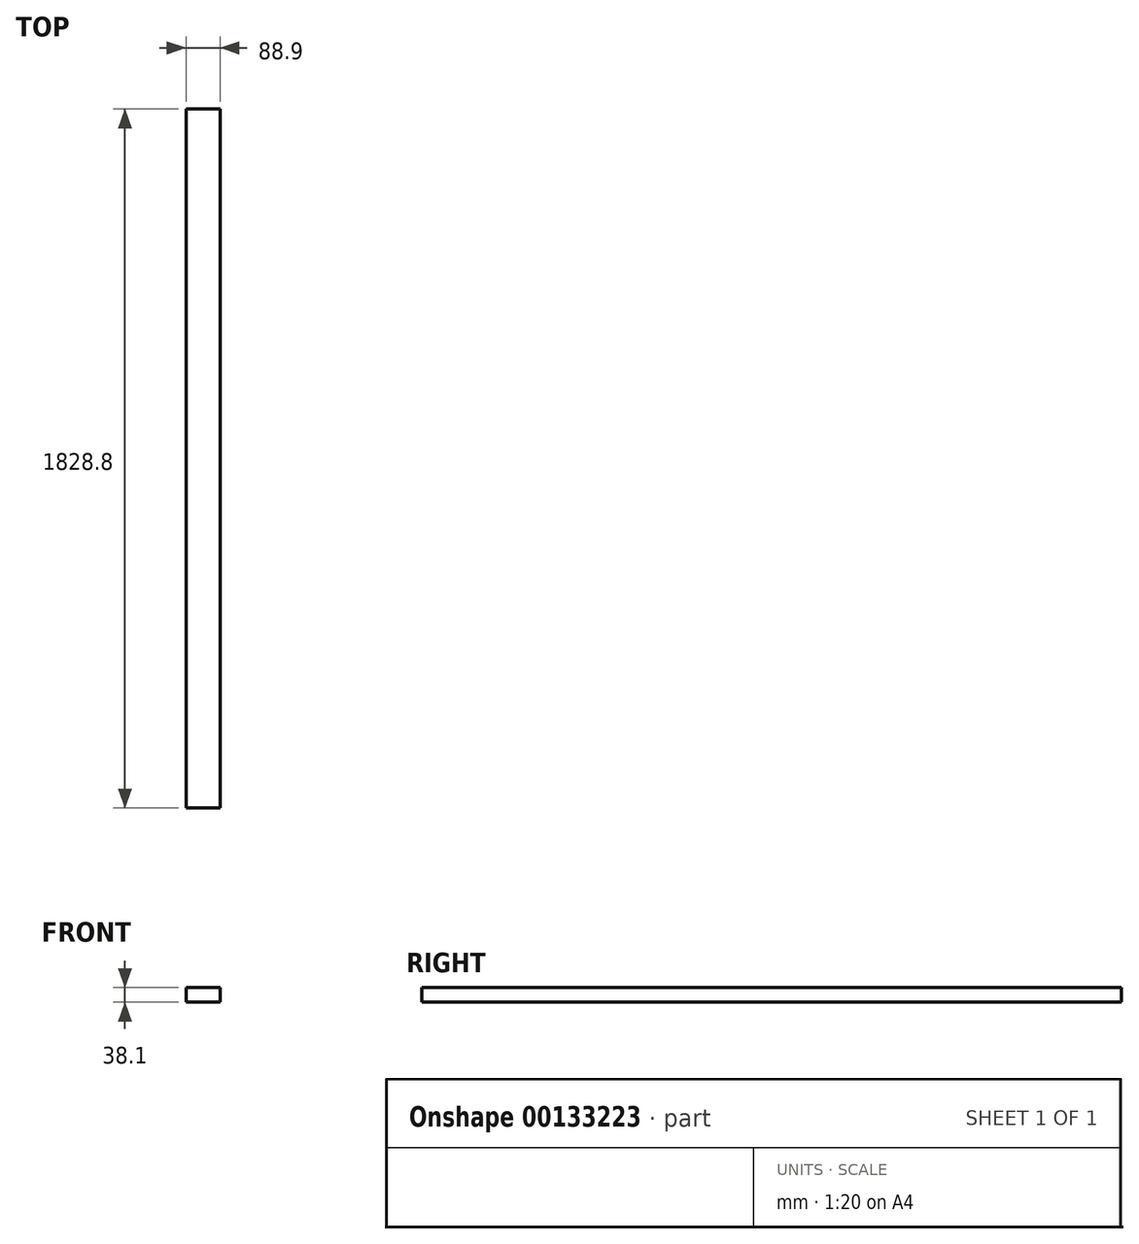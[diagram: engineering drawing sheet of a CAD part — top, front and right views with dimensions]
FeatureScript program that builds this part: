
annotation { "Feature Type Name" : "Feature", "Feature Type Description" : "" }
export const myFeature = defineFeature(function(context is Context, id is Id, definition is map)
    precondition{}
    {
        {
            var Q0;
            Q0=qCreatedBy(makeId("Front.planeOp"),FACE);
            var sketch = newSketch(context, id + "F0", { "sketchPlane" : qUnion([Q0])});
            skLineSegment(sketch, "E0.bottom", {"start": v(0, 0) * mm, "end": v(88.9, 0) * mm});
            skLineSegment(sketch, "E0.top", {"start": v(0, 38.1) * mm, "end": v(88.9, 38.1) * mm});
            skLineSegment(sketch, "E0.left", {"start": v(0, 0) * mm, "end": v(0, 38.1) * mm});
            skLineSegment(sketch, "E0.right", {"start": v(88.9, 0) * mm, "end": v(88.9, 38.1) * mm});
            skSolve(sketch);
        }
        {
            var Q0;
            Q0 = qSketchRegion(id + "F0", true);
            extrude(context, id + "F1", {"entities" : qUnion([Q0]), "depth" : 1828.8 * mm});
        }
        {
            var Q0;
            Q0=makeQuery(id+"F1.opExtrude","SWEPT_BODY",BODY,{"disambiguationData":[OSD([sQuery(id+"F0.wireOp",EDGE,"E0.bottom"),sQuery(id+"F0.wireOp",EDGE,"E0.top"),sQuery(id+"F0.wireOp",EDGE,"E0.left"),sQuery(id+"F0.wireOp",EDGE,"E0.right")])]});
            transform(context, id + "F2", {"entities" : qUnion([Q0]), "transformType" : TransformType.TRANSLATION_3D, "dx" : 203.2 * mm, "dy" : 0 * mm, "dz" : 0 * mm, "makeCopy" : true});
        }
        {
            var Q0;
            Q0=makeQuery(id+"F2.opPattern","COPY",BODY,{"derivedFrom":makeQuery(id+"F1.opExtrude","SWEPT_BODY",BODY,{"disambiguationData":[OSD([sQuery(id+"F0.wireOp",EDGE,"E0.bottom"),sQuery(id+"F0.wireOp",EDGE,"E0.top"),sQuery(id+"F0.wireOp",EDGE,"E0.left"),sQuery(id+"F0.wireOp",EDGE,"E0.right")])]}),"instanceName":"1"});
            deleteBodies(context, id + "F3", {"entities" : qUnion([Q0])});
        }
    });
